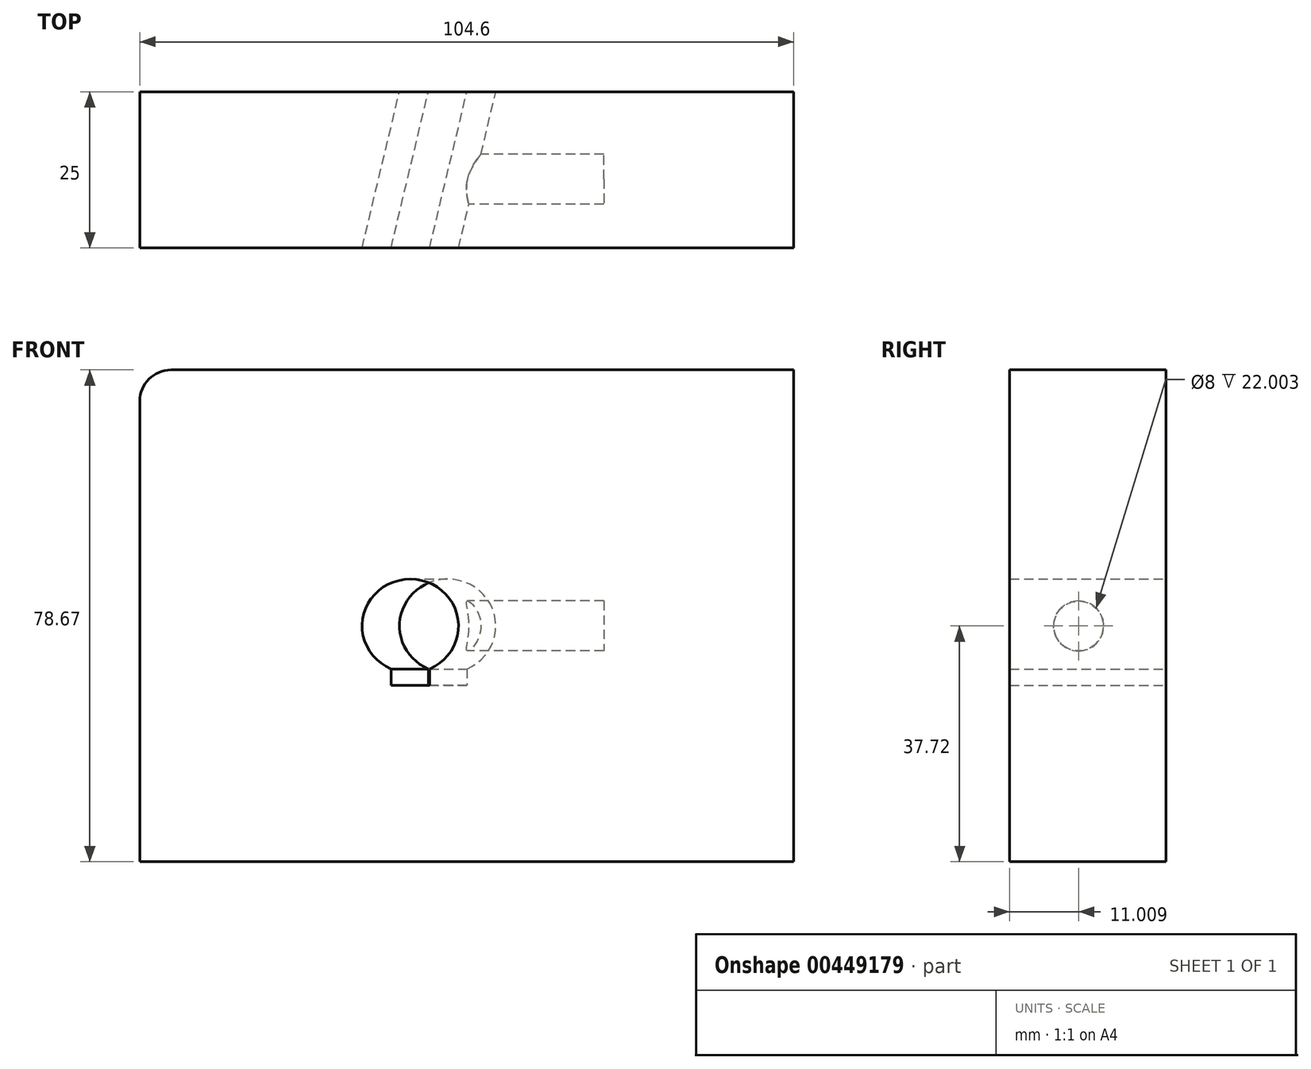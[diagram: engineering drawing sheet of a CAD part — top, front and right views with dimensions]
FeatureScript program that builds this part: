
annotation { "Feature Type Name" : "Feature", "Feature Type Description" : "" }
export const myFeature = defineFeature(function(context is Context, id is Id, definition is map)
    precondition{}
    {
        {
            var Q0;
            Q0=qCreatedBy(makeId("Front.planeOp"),FACE);
            var sketch = newSketch(context, id + "F0", { "sketchPlane" : qUnion([Q0])});
            skLineSegment(sketch, "E0", {"start": v(-44.24, 40.95) * mm, "end": v(55.36, 40.95) * mm});
            skLineSegment(sketch, "E1", {"start": v(55.36, 40.95) * mm, "end": v(55.36, -37.72) * mm});
            skLineSegment(sketch, "E2", {"start": v(55.36, -37.72) * mm, "end": v(-49.24, -37.72) * mm});
            skLineSegment(sketch, "E3", {"start": v(-49.24, -37.72) * mm, "end": v(-49.24, 35.95) * mm});
            skPoint(sketch, "E4.visualSharp", {"position": v(-49.24, 40.95) * mm});
            skArc(sketch, "E4.filletArc", {"start": v(-44.24, 40.95) * mm, "mid": v(-47.77, 39.49) * mm, "end": v(-49.24, 35.95) * mm});
            skSolve(sketch);
        }
        {
            var Q0;
            Q0=makeQuery(id+"F0.imprint","IMPRINT",FACE,{"disambiguationData":[TD([[makeQuery(id+"F0.imprint","IMPRINT",EDGE,{"derivedFrom":sQuery(id+"F0.wireOp",EDGE,"E0")}),-1.0]])]});
            extrude(context, id + "F1", {"entities" : qUnion([Q0]), "depth" : 25 * mm});
        }
        {
            var Q0;
            Q0=makeQuery(id+"F1.opExtrude","CAP_VERTEX",VERTEX,{"disambiguationData":[OSD([sQuery(id+"F0.wireOp",EDGE,"E3"),sQuery(id+"F0.wireOp",EDGE,"E4.filletArc")])],"isStart":true});
            var Q1;
            Q1=makeQuery(id+"F1.opExtrude","CAP_VERTEX",VERTEX,{"disambiguationData":[OSD([sQuery(id+"F0.wireOp",EDGE,"E2"),sQuery(id+"F0.wireOp",EDGE,"E3")])],"isStart":true});
            var Q2;
            Q2=makeQuery(id+"F1.opExtrude","CAP_VERTEX",VERTEX,{"disambiguationData":[OSD([sQuery(id+"F0.wireOp",EDGE,"E1"),sQuery(id+"F0.wireOp",EDGE,"E2")])],"isStart":false});
            cPlane(context, id + "F2", {"entities" : qUnion([Q0, Q1, Q2]), "cplaneType" : CPlaneType.THREE_POINT, "offset" : 25 * mm, "width" : 150 * mm, "height" : 150 * mm});
        }
        {
            var Q0;
            Q0=qCreatedBy(id+"F2.planeOp",FACE);
            var sketch = newSketch(context, id + "F3", { "sketchPlane" : qUnion([Q0])});
            skArc(sketch, "E5", {"start": v(3, -6.87) * mm, "mid": v(0, 7.5) * mm, "end": v(-3, -6.87) * mm});
            skLineSegment(sketch, "E6", {"start": v(3, -6.87) * mm, "end": v(3, -9.5) * mm});
            skLineSegment(sketch, "E7", {"start": v(3, -9.5) * mm, "end": v(-3, -9.5) * mm});
            skLineSegment(sketch, "E8", {"start": v(-3, -9.5) * mm, "end": v(-3, -6.87) * mm});
            skLineSegment(sketch, "E9", {"start": v(0, -9.5) * mm, "end": v(0, 0) * mm, "construction": true});
            skSolve(sketch);
        }
        {
            var Q0;
            Q0=makeQuery(id+"F3.imprint","IMPRINT",FACE,{"disambiguationData":[TD([[makeQuery(id+"F3.imprint","IMPRINT",EDGE,{"derivedFrom":sQuery(id+"F3.wireOp",EDGE,"E5")}),1.0]])]});
            extrude(context, id + "F4", {"entities" : qUnion([Q0]), "operationType" : NewBodyOperationType.REMOVE, "endBound" : BoundingType.THROUGH_ALL, "oppositeDirection" : true, "depth" : 25 * mm, "hasSecondDirection" : true, "secondDirectionBound" : SecondDirectionBoundingType.THROUGH_ALL, "secondDirectionOppositeDirection" : false, "secondDirectionDepth" : 25 * mm});
        }
        {
            var Q0;
            Q0=qCreatedBy(makeId("Right.planeOp"),FACE);
            var sketch = newSketch(context, id + "F5", { "sketchPlane" : qUnion([Q0])});
            skCircle(sketch, "E10", {"center": v(-14, 0) * mm, "radius": 4 * mm});
            skSolve(sketch);
        }
        {
            var Q0;
            Q0=makeQuery(id+"F5.imprint","IMPRINT",FACE,{"disambiguationData":[TD([[makeQuery(id+"F5.imprint","IMPRINT",EDGE,{"derivedFrom":sQuery(id+"F5.wireOp",EDGE,"E10")}),1.0]])]});
            extrude(context, id + "F6", {"entities" : qUnion([Q0]), "operationType" : NewBodyOperationType.REMOVE, "depth" : 25 * mm});
        }
    });
